# Revit family: Ограждение_Панель_В рамке_2500
name_source: partatom
category: Специальное оборудование
units: mm (PartAtom-declared; Revit-internal decimal feet)

## family parameters
Общий = Нет
При загрузке вырезать с полостями = Нет
Размер круглого соединителя = Использовать диаметр
Тип детали = Нормальный
Точка расчета площади = Нет

## types (4) — shared parameters
ADSK_Единица измерения = м.
ADSK_Завод-изготовитель = FENSYS
URL = https://www.fensys.ru
Глубина столба = 80 мм
Группа модели = Ограждение
Изготовитель = FENSYS
Отступ панели = 40 мм
Отступ панели от основания = 70 мм
Толщина стенки столба = 3 мм
Ширина панели = 2500 мм
Ширина столба = 80 мм

## per-type parameters (varying)
| type | Код по классификатору | Наименование | Описание | Размер прутка | Стоимость | Толщина профиля рамки |
| Панель_2500_Рамка 60х40х3_Пруток d5 | 33747 | Панель в рамке Тип 1.3.: HxW (высота х ширина) 2000x2500 мм,  рамка: профиль 60х40 мм, заполнение: панель с ячейкой = 50x150 мм, проволока D6 мм, габариты  (высота х ширина) 1 988x2 395 мм | Тип 1.3 | 6 | 17.5 $ | 3 |
| Панель_2500_Рамка 60х40х2_Пруток d5 | 13599N | Ограждение - Панель 2500_Фланцевое крепление_Столб 80х80 | Тип 1.2 | 5 | 6.1 $ | 2 |
| Панель_2500_Рамка 60х40х2_Пруток d6 | 13599N | Ограждение - Панель 2500_Фланцевое крепление_Столб 80х80 | Тип 1.2 | 6 | 6.1 $ | 2 |
| Панель_2500_Рамка 60х40х3_Пруток d6 | 33747 | Панель в рамке Тип 1.3.: HxW (высота х ширина) 2000x2500 мм,  рамка: профиль 60х40 мм, заполнение: панель с ячейкой = 50x150 мм, проволока D6 мм, габариты  (высота х ширина) 1 988x2 395 мм | Тип 1.3 | 6 | 17.5 $ | 3 |
